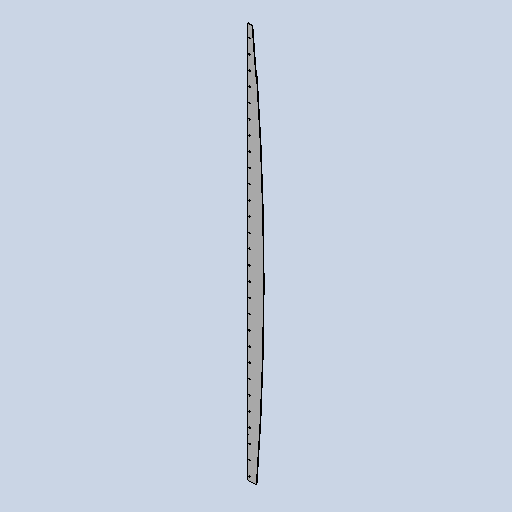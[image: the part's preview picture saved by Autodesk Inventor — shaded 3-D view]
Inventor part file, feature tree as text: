
AUTODESK INVENTOR PART (.ipt)
format: ipt  version: 2025 (Build 290162010, 162A)  size: 219,136 bytes
history: native  units: mm
features: sketch x2, other x2, sheet_metal_op x1, extrude x1, pattern_linear x1, projected_geometry x1
ambient origin geometry x8: Origin, YZ Plane, XZ Plane, XY Plane, X Axis, Y Axis, Z Axis, Center Point
bodies: Body1 (feature_tree)
feature tree (8):
  sheet_metal_op  "Face1"
  extrude  "Extrusion2"  Depth=3.0mm
  pattern_linear  "Rectangular Pattern1"  Spacing1=3.0mm  [1 undecoded]
  sketch  "Sketch1"  dims[d65=8.0mm d78=3.0mm]
  other  "Plate3"
  sketch  "Sketch3"  dims[d80=3.0mm d115=3.0mm d120=3.0mm d131=11050.0mm d132=25.0mm d133=42.0mm d134=1970.0mm d135=7.0mm d136=8.0mm d137=20.0mm d138=10.0mm d139=0.0mm d140=310.0mm d142=70.0mm d143=10.0mm d145=4.0mm d146=210.0mm d147=4.0mm]
  projected_geometry  "Projected Loop1"
  other  "Definition1"
note: 1 required parameter value undecoded (feature->parameter linkage not recoverable at this tier; creation-order binding heuristic only, values carry confidence <= 0.55)
